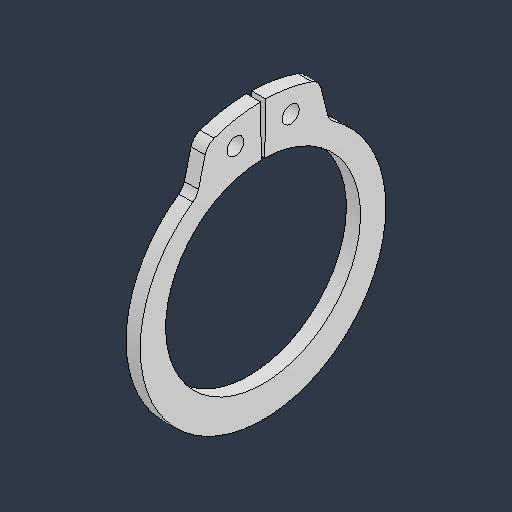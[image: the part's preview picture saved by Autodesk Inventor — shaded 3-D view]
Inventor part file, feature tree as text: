
AUTODESK INVENTOR PART (.ipt)
format: ipt  version: 2024.3 (Build 283343000, 343)  size: 110,080 bytes
history: native  units: in
note: dims shown in document units (in); Inventor stores cm internally (conversion verified against a paired STEP export)
features: fillet x1
ambient origin geometry x8: Origin, YZ Plane, XZ Plane, XY Plane, X Axis, Y Axis, Z Axis, Center Point
bodies: Solid1 (feature_tree)
feature tree (1):
  fillet  "Fillet1"  [1 undecoded]
note: 1 required parameter value undecoded (feature->parameter linkage not recoverable at this tier; creation-order binding heuristic only, values carry confidence <= 0.55)
